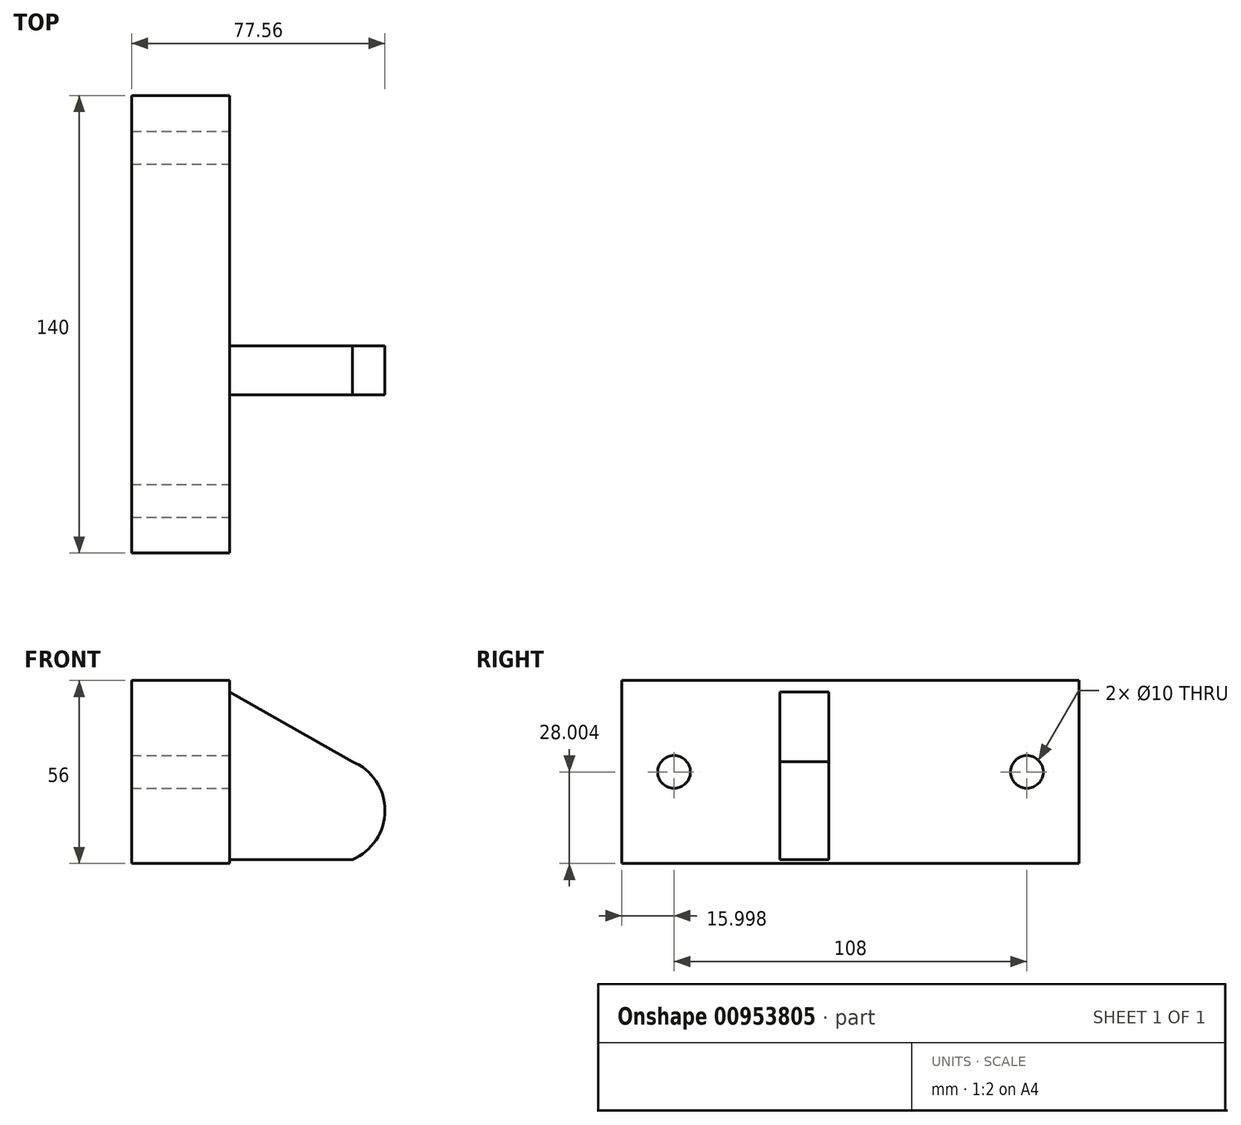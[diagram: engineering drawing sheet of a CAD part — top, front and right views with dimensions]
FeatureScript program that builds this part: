
annotation { "Feature Type Name" : "Feature", "Feature Type Description" : "" }
export const myFeature = defineFeature(function(context is Context, id is Id, definition is map)
    precondition{}
    {
        {
            var Q0;
            Q0=qCreatedBy(makeId("Right.planeOp"),FACE);
            var sketch = newSketch(context, id + "F0", { "sketchPlane" : qUnion([Q0])});
            skLineSegment(sketch, "E0.bottom", {"start": v(-63.4, 21.12) * mm, "end": v(76.6, 21.12) * mm});
            skLineSegment(sketch, "E0.top", {"start": v(-63.4, -34.88) * mm, "end": v(76.6, -34.88) * mm});
            skLineSegment(sketch, "E0.left", {"start": v(-63.4, 21.12) * mm, "end": v(-63.4, -34.88) * mm});
            skLineSegment(sketch, "E0.right", {"start": v(76.6, 21.12) * mm, "end": v(76.6, -34.88) * mm});
            skSolve(sketch);
        }
        {
            var Q0;
            Q0 = qSketchRegion(id + "F0", true);
            extrude(context, id + "F1", {"entities" : qUnion([Q0]), "depth" : 30 * mm, "offsetDistance" : 25.4 * mm});
        }
        {
            var Q0;
            Q0=makeQuery(id+"F1.opExtrude","CAP_FACE",FACE,{"disambiguationData":[OSD([sQuery(id+"F0.wireOp",EDGE,"E0.bottom"),sQuery(id+"F0.wireOp",EDGE,"E0.top"),sQuery(id+"F0.wireOp",EDGE,"E0.left"),sQuery(id+"F0.wireOp",EDGE,"E0.right")])],"isStart":false});
            var sketch = newSketch(context, id + "F2", { "sketchPlane" : qUnion([Q0])});
            skCircle(sketch, "E1", {"center": v(-47.4, -6.88) * mm, "radius": 5 * mm});
            skSolve(sketch);
        }
        {
            var Q0;
            Q0=makeQuery(id+"F2.imprint","IMPRINT",FACE,{"disambiguationData":[TD([[makeQuery(id+"F2.imprint","IMPRINT",EDGE,{"derivedFrom":sQuery(id+"F2.wireOp",EDGE,"E1")}),-1.0]])]});
            var sketch = newSketch(context, id + "F3", { "sketchPlane" : qUnion([Q0])});
            skCircle(sketch, "E2", {"center": v(60.6, -6.88) * mm, "radius": 5 * mm});
            skSolve(sketch);
        }
        {
            var Q0;
            Q0=sQuery(id+"F2.wireOp",VERTEX,"E1.center");
            var Q1;
            Q1=makeQuery(id+"F1.opExtrude","SWEPT_BODY",BODY,{"disambiguationData":[OSD([sQuery(id+"F0.wireOp",EDGE,"E0.bottom"),sQuery(id+"F0.wireOp",EDGE,"E0.top"),sQuery(id+"F0.wireOp",EDGE,"E0.left"),sQuery(id+"F0.wireOp",EDGE,"E0.right")])]});
            hole(context, id + "F4", {"style" : HoleStyle.SIMPLE, "endStyle" : HoleEndStyle.THROUGH, "holeDiameter" : 10 * mm, "majorDiameter" : 6.35 * mm, "isTappedThrough" : true, "tappedDepth" : 12.7 * mm, "tapClearance" : 3, "locations" : qUnion([Q0]), "scope" : qUnion([Q1])});
        }
        {
            var Q0;
            Q0=sQuery(id+"F3.wireOp",VERTEX,"E2.center");
            var Q1;
            Q1=makeQuery(id+"F1.opExtrude","SWEPT_BODY",BODY,{"disambiguationData":[OSD([sQuery(id+"F0.wireOp",EDGE,"E0.bottom"),sQuery(id+"F0.wireOp",EDGE,"E0.top"),sQuery(id+"F0.wireOp",EDGE,"E0.left"),sQuery(id+"F0.wireOp",EDGE,"E0.right")])]});
            hole(context, id + "F5", {"style" : HoleStyle.SIMPLE, "endStyle" : HoleEndStyle.THROUGH, "holeDiameter" : 10 * mm, "majorDiameter" : 6.35 * mm, "isTappedThrough" : true, "tappedDepth" : 12.7 * mm, "tapClearance" : 3, "locations" : qUnion([Q0]), "scope" : qUnion([Q1])});
        }
        {
            var Q0;
            Q0=qCreatedBy(makeId("Front.planeOp"),FACE);
            var sketch = newSketch(context, id + "F6", { "sketchPlane" : qUnion([Q0])});
            skLineSegment(sketch, "E3.bottom", {"start": v(27.56, -3.7) * mm, "end": v(67.56, -3.7) * mm});
            skLineSegment(sketch, "E3.top", {"start": v(27.56, -33.7) * mm, "end": v(67.56, -33.7) * mm});
            skLineSegment(sketch, "E3.left", {"start": v(27.56, -3.7) * mm, "end": v(27.56, -33.7) * mm});
            skLineSegment(sketch, "E3.right", {"start": v(67.56, -3.7) * mm, "end": v(67.56, -33.7) * mm});
            skLineSegment(sketch, "E4", {"start": v(30.33, -3.7) * mm, "end": v(67.56, -3.7) * mm});
            skArc(sketch, "E5", {"start": v(67.56, -33.7) * mm, "mid": v(77.56, -18.7) * mm, "end": v(67.56, -3.7) * mm});
            skLineSegment(sketch, "E6", {"start": v(27.56, -3.7) * mm, "end": v(27.56, 19) * mm});
            skLineSegment(sketch, "E7", {"start": v(27.56, 19) * mm, "end": v(67.56, -3.7) * mm});
            skSolve(sketch);
        }
        {
            var Q0;
            Q0 = qSketchRegion(id + "F6", true);
            extrude(context, id + "F7", {"entities" : qUnion([Q0]), "operationType" : NewBodyOperationType.ADD, "depth" : 15 * mm, "offsetDistance" : 25.4 * mm});
        }
    });
